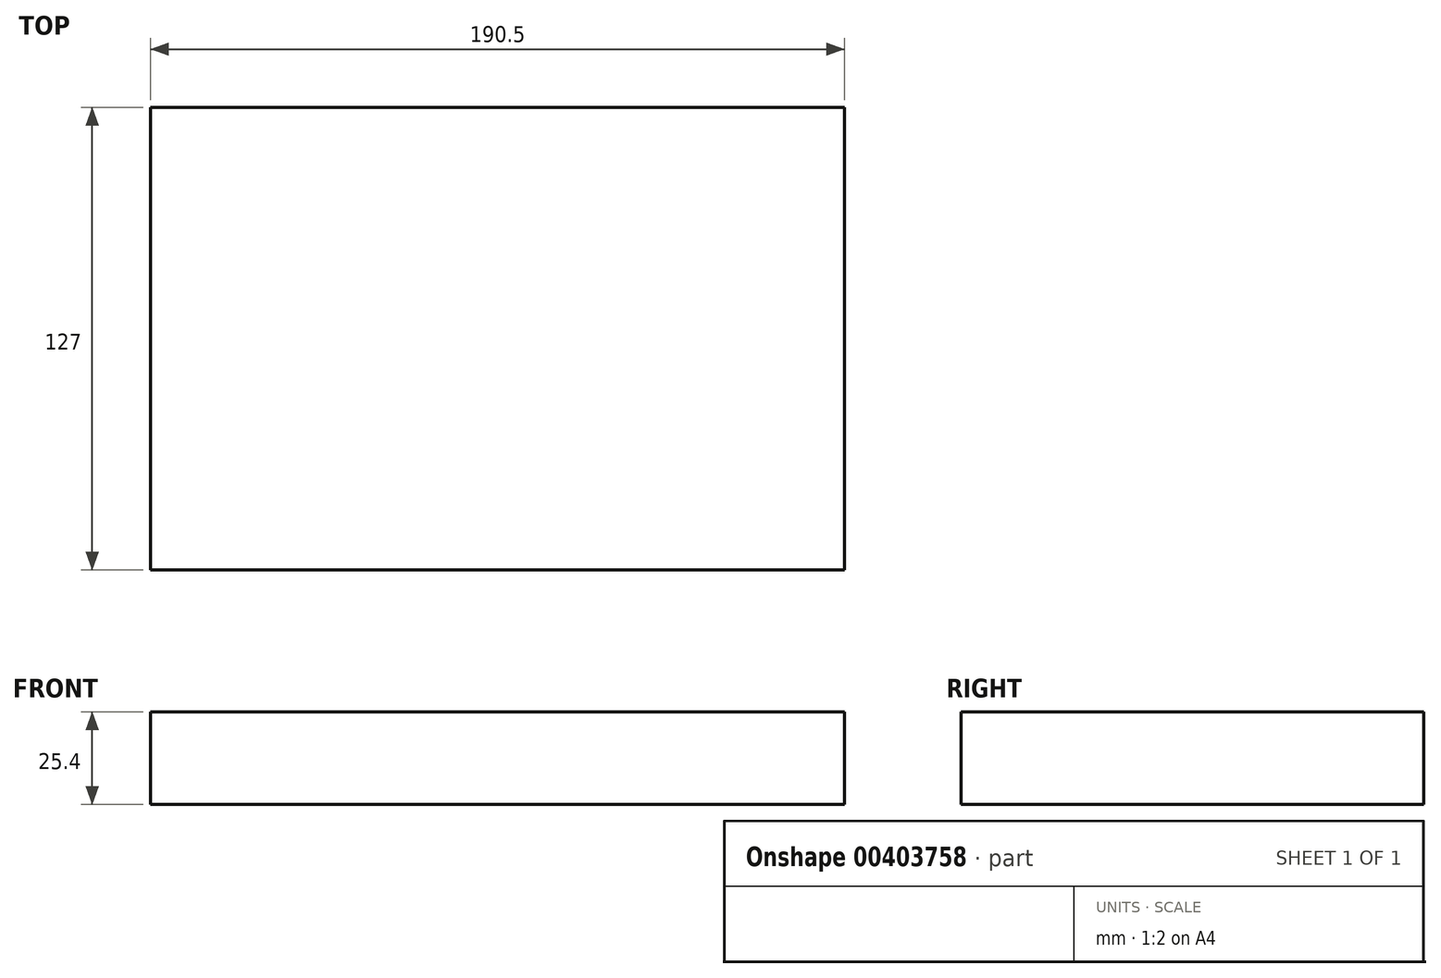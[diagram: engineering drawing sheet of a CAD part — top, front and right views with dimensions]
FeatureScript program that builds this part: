
annotation { "Feature Type Name" : "Feature", "Feature Type Description" : "" }
export const myFeature = defineFeature(function(context is Context, id is Id, definition is map)
    precondition{}
    {
        {
            var Q0;
            Q0=qCreatedBy(makeId("Top.planeOp"),FACE);
            var sketch = newSketch(context, id + "F0", { "sketchPlane" : qUnion([Q0])});
            skLineSegment(sketch, "E0.bottom", {"start": v(-95.25, 63.5) * mm, "end": v(95.25, 63.5) * mm});
            skLineSegment(sketch, "E0.top", {"start": v(-95.25, -63.5) * mm, "end": v(95.25, -63.5) * mm});
            skLineSegment(sketch, "E0.left", {"start": v(-95.25, 63.5) * mm, "end": v(-95.25, -63.5) * mm});
            skLineSegment(sketch, "E0.right", {"start": v(95.25, 63.5) * mm, "end": v(95.25, -63.5) * mm});
            skPoint(sketch, "E0.middle", {"position": v(0, 0) * mm});
            skSolve(sketch);
        }
        {
            var Q0;
            Q0 = qSketchRegion(id + "F0", true);
            extrude(context, id + "F1", {"entities" : qUnion([Q0]), "depth" : 25.4 * mm, "offsetDistance" : 25.4 * mm});
        }
    });
